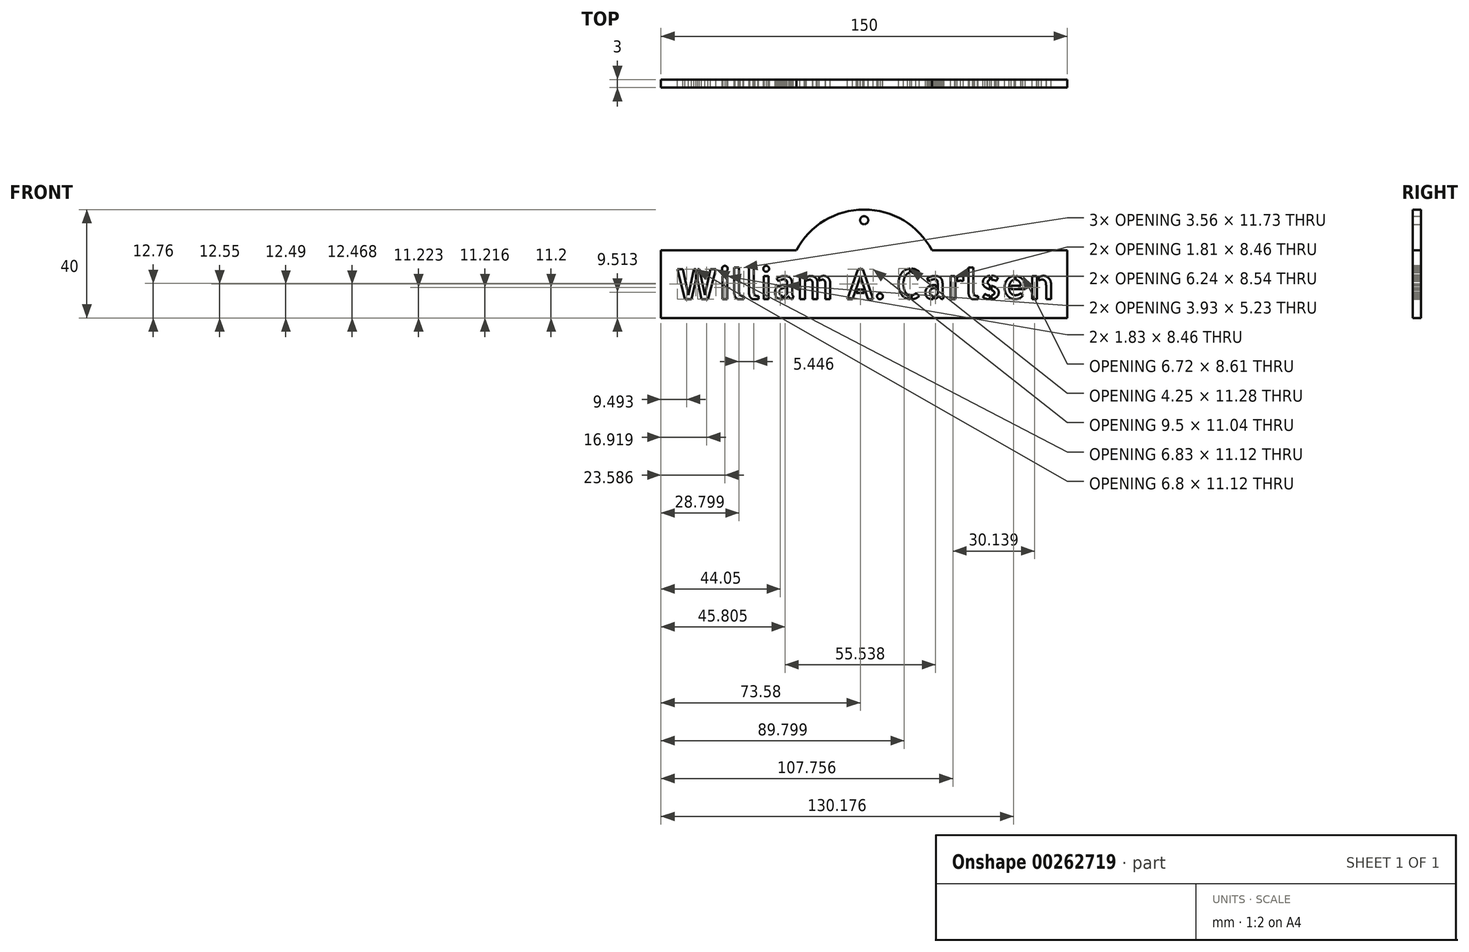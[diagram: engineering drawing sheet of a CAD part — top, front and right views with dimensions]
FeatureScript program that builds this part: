
annotation { "Feature Type Name" : "Feature", "Feature Type Description" : "" }
export const myFeature = defineFeature(function(context is Context, id is Id, definition is map)
    precondition{}
    {
        {
            var Q0;
            Q0=qCreatedBy(makeId("Front.planeOp"),FACE);
            var sketch = newSketch(context, id + "F0", { "sketchPlane" : qUnion([Q0])});
            skLineSegment(sketch, "E0.top", {"start": v(-45.32, -29.07) * mm, "end": v(104.68, -29.07) * mm});
            skLineSegment(sketch, "E0.left", {"start": v(-45.32, -4.07) * mm, "end": v(-45.32, -29.07) * mm});
            skLineSegment(sketch, "E0.right", {"start": v(104.68, -4.07) * mm, "end": v(104.68, -29.07) * mm});
            skLineSegment(sketch, "E1", {"start": v(-45.32, -4.07) * mm, "end": v(4.68, -4.07) * mm});
            skLineSegment(sketch, "E2", {"start": v(104.68, -4.07) * mm, "end": v(54.68, -4.07) * mm});
            skText(sketch, "E3", { "text": "William A. Carlsen\n", "fontName": "AllertaStencil-Regular.ttf"});
            skCircle(sketch, "E4", {"center": v(29.68, 6.98) * mm, "radius": 1.5 * mm});
            skPoint(sketch, "E5", {"position": v(29.68, -29.07) * mm});
            skPoint(sketch, "E6", {"position": v(-45.32, -16.57) * mm});
            skPoint(sketch, "E7", {"position": v(104.68, -16.57) * mm});
            skPoint(sketch, "E8", {"position": v(29.68, -16.57) * mm});
            skArc(sketch, "E9", {"start": v(54.68, -4.07) * mm, "mid": v(29.68, 10.93) * mm, "end": v(4.68, -4.07) * mm});
            const initialGuessF0  = {"E3": [-0.04032, -0.0221, 1, 0, 0.01106]};
            skSetInitialGuess(sketch, initialGuessF0);
            skSolve(sketch);
        }
        {
            var Q0;
            Q0 = qSketchRegion(id + "F0", true);
            extrude(context, id + "F1", {"entities" : qUnion([Q0]), "depth" : 3 * mm});
        }
    });
